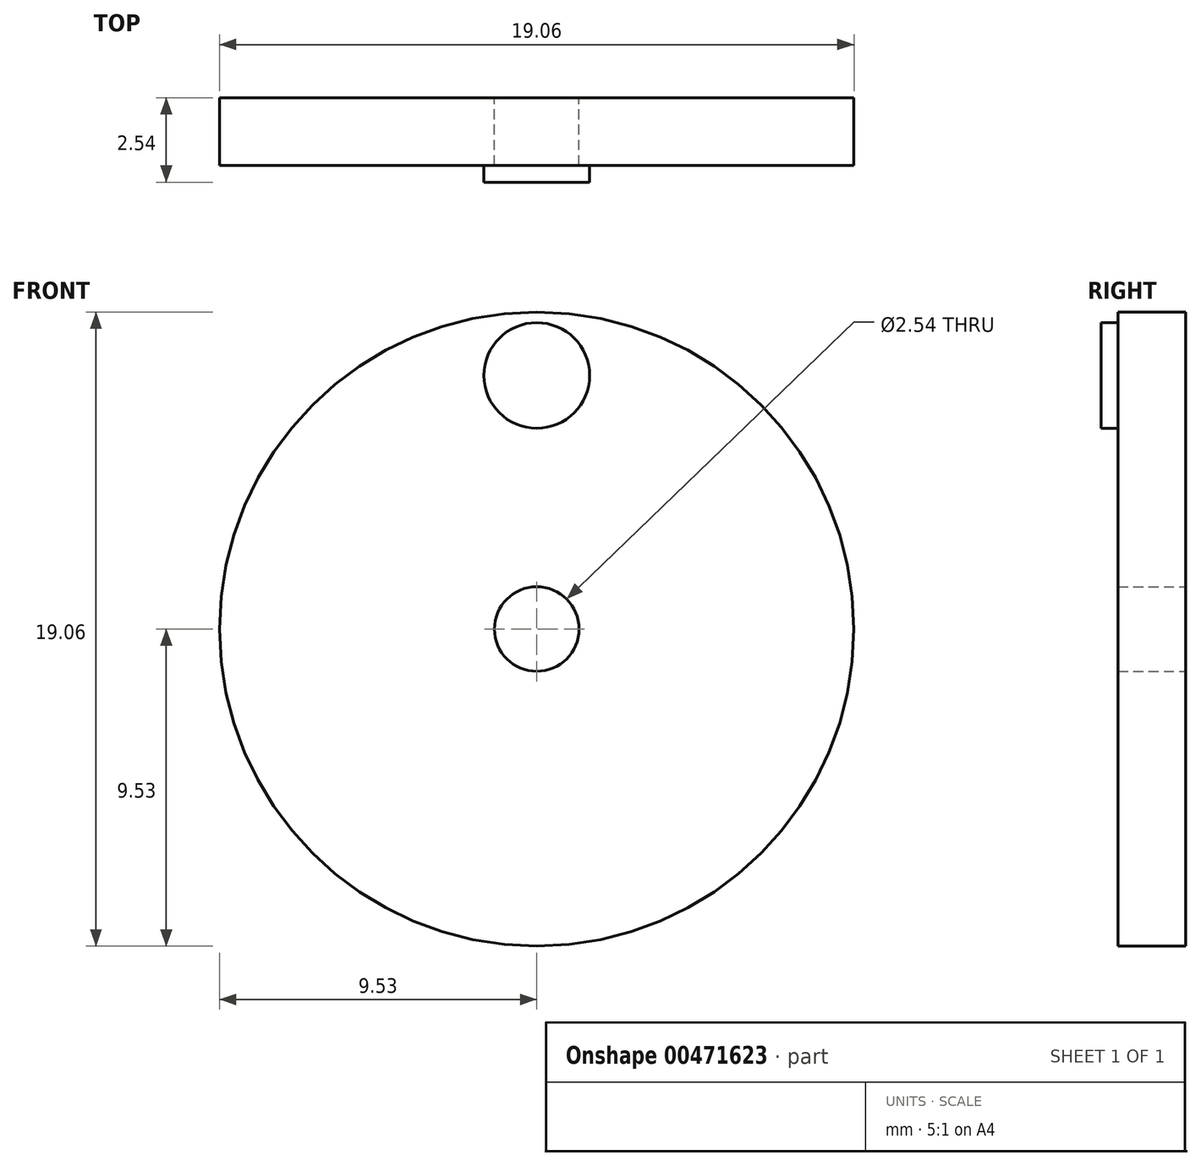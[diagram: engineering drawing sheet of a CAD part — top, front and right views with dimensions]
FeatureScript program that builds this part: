
annotation { "Feature Type Name" : "Feature", "Feature Type Description" : "" }
export const myFeature = defineFeature(function(context is Context, id is Id, definition is map)
    precondition{}
    {
        {
            var Q0;
            Q0=qCreatedBy(makeId("Front.planeOp"),FACE);
            var sketch = newSketch(context, id + "F0", { "sketchPlane" : qUnion([Q0])});
            skCircle(sketch, "E0", {"center": v(0, 7.62) * mm, "radius": 1.59 * mm});
            skLineSegment(sketch, "E1", {"start": v(0, 26.63) * mm, "end": v(0, -23.82) * mm, "construction": true});
            skLineSegment(sketch, "E2", {"start": v(-28.36, 0) * mm, "end": v(35.16, 0) * mm, "construction": true});
            skSolve(sketch);
        }
        {
            var Q0;
            Q0=qCreatedBy(makeId("Front.planeOp"),FACE);
            var sketch = newSketch(context, id + "F1", { "sketchPlane" : qUnion([Q0])});
            skCircle(sketch, "E3", {"center": v(0, 0) * mm, "radius": 9.53 * mm});
            skCircle(sketch, "E4", {"center": v(0, 0) * mm, "radius": 1.27 * mm});
            skSolve(sketch);
        }
        {
            var Q0;
            Q0=makeQuery(id+"F1.imprint","IMPRINT",FACE,{"disambiguationData":[TD([[makeQuery(id+"F1.imprint","IMPRINT",EDGE,{"derivedFrom":sQuery(id+"F1.wireOp",EDGE,"E3")}),1.0]])]});
            extrude(context, id + "F2", {"entities" : qUnion([Q0]), "depth" : 2.03 * mm});
        }
        {
            var Q0;
            Q0 = qSketchRegion(id + "F0", true);
            extrude(context, id + "F3", {"entities" : qUnion([Q0]), "operationType" : NewBodyOperationType.ADD, "depth" : 2.54 * mm});
        }
    });
